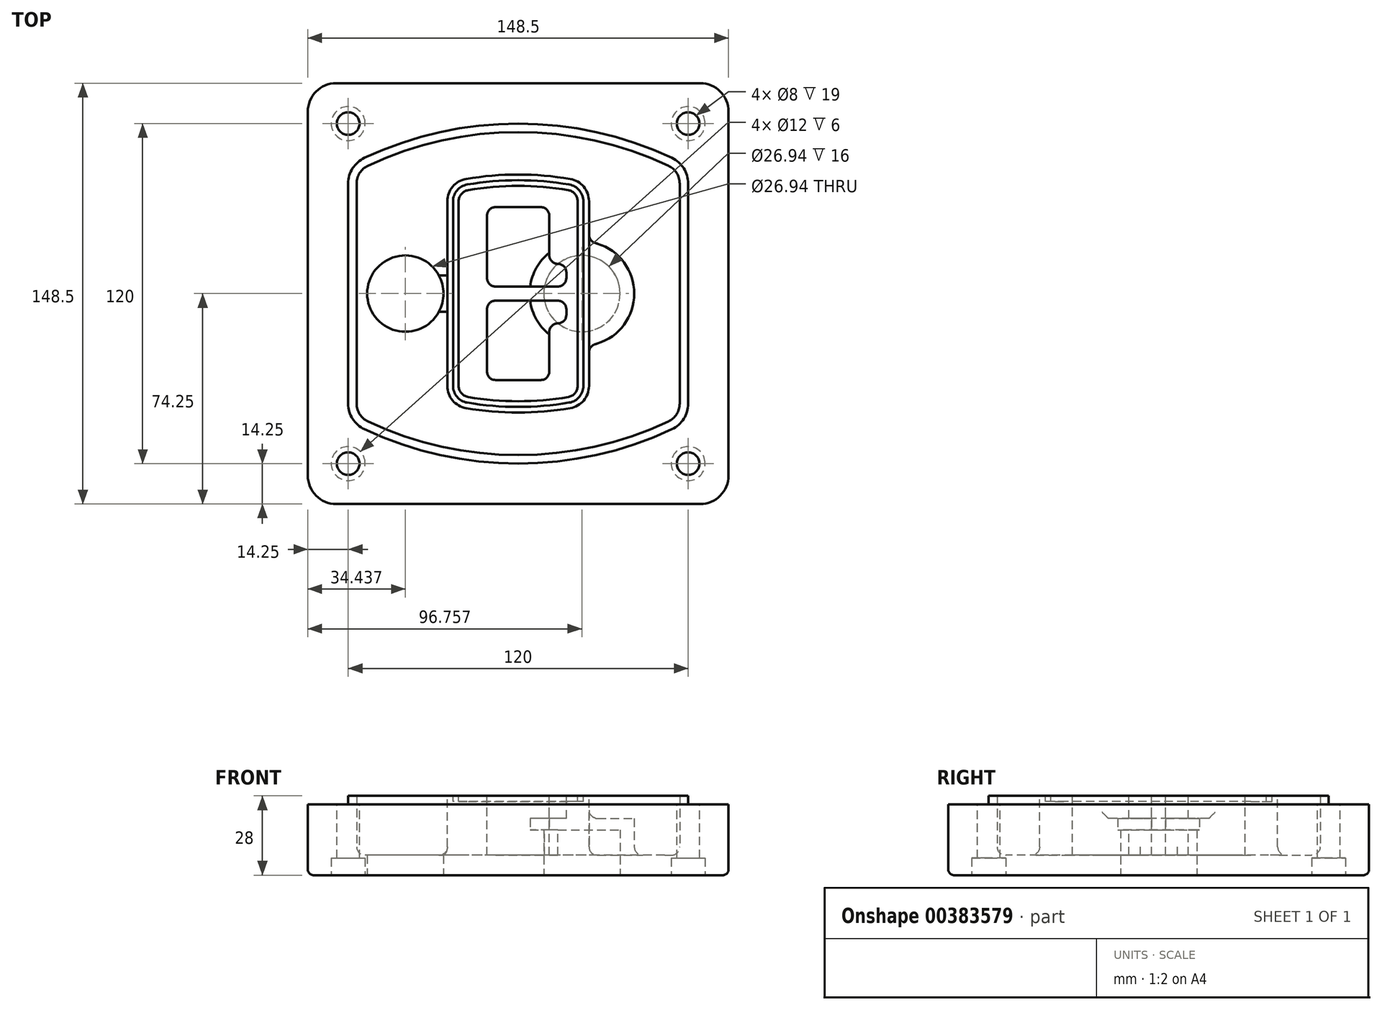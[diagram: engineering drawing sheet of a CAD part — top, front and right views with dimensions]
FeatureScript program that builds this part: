
annotation { "Feature Type Name" : "Feature", "Feature Type Description" : "" }
export const myFeature = defineFeature(function(context is Context, id is Id, definition is map)
    precondition{}
    {
        {
            var Q0;
            Q0=qCreatedBy(makeId("Top.planeOp"),FACE);
            var sketch = newSketch(context, id + "F0", { "sketchPlane" : qUnion([Q0])});
            skPoint(sketch, "E0.rect.middle", {"position": v(0, 0) * mm});
            skLineSegment(sketch, "E1.bottom", {"start": v(-64.25, -74.25) * mm, "end": v(64.25, -74.25) * mm});
            skLineSegment(sketch, "E1.top", {"start": v(-64.25, 74.25) * mm, "end": v(64.25, 74.25) * mm});
            skLineSegment(sketch, "E1.left", {"start": v(-74.25, -64.25) * mm, "end": v(-74.25, 64.25) * mm});
            skLineSegment(sketch, "E1.right", {"start": v(74.25, -64.25) * mm, "end": v(74.25, 64.25) * mm});
            skLineSegment(sketch, "E2", {"start": v(-74.25, 74.25) * mm, "end": v(74.25, -74.25) * mm, "construction": true});
            skLineSegment(sketch, "E3", {"start": v(74.25, 74.25) * mm, "end": v(-74.25, -74.25) * mm, "construction": true});
            skCircle(sketch, "E4", {"center": v(-60, 60) * mm, "radius": 4 * mm});
            skCircle(sketch, "E5", {"center": v(60, 60) * mm, "radius": 4 * mm});
            skCircle(sketch, "E6", {"center": v(60, -60) * mm, "radius": 4 * mm});
            skCircle(sketch, "E7", {"center": v(-60, -60) * mm, "radius": 4 * mm});
            skLineSegment(sketch, "E8", {"start": v(-60, 60) * mm, "end": v(60, 60) * mm, "construction": true});
            skLineSegment(sketch, "E9", {"start": v(60, 60) * mm, "end": v(60, -60) * mm, "construction": true});
            skLineSegment(sketch, "E10", {"start": v(60, -60) * mm, "end": v(-60, -60) * mm, "construction": true});
            skLineSegment(sketch, "E11", {"start": v(-60, -60) * mm, "end": v(-60, 60) * mm, "construction": true});
            skLineSegment(sketch, "E12", {"start": v(-60, 38.83) * mm, "end": v(-60, -38.83) * mm});
            skLineSegment(sketch, "E13", {"start": v(60, 38.83) * mm, "end": v(60, -38.83) * mm});
            skArc(sketch, "E14", {"start": v(54.26, 47.88) * mm, "mid": v(0, 60) * mm, "end": v(-54.26, 47.88) * mm});
            skArc(sketch, "E15", {"start": v(-54.26, -47.88) * mm, "mid": v(0, -60) * mm, "end": v(54.26, -47.88) * mm});
            skLineSegment(sketch, "E16", {"start": v(-60, 0) * mm, "end": v(60, 0) * mm, "construction": true});
            skPoint(sketch, "E17.visualSharp", {"position": v(-60, -45) * mm});
            skArc(sketch, "E17.filletArc", {"start": v(-60, -38.83) * mm, "mid": v(-58.44, -44.2) * mm, "end": v(-54.26, -47.88) * mm});
            skPoint(sketch, "E18.visualSharp", {"position": v(-60, 45) * mm});
            skArc(sketch, "E18.filletArc", {"start": v(-54.26, 47.88) * mm, "mid": v(-58.44, 44.2) * mm, "end": v(-60, 38.83) * mm});
            skPoint(sketch, "E19.visualSharp", {"position": v(60, 45) * mm});
            skArc(sketch, "E19.filletArc", {"start": v(60, 38.83) * mm, "mid": v(58.44, 44.2) * mm, "end": v(54.26, 47.88) * mm});
            skPoint(sketch, "E20.visualSharp", {"position": v(60, -45) * mm});
            skArc(sketch, "E20.filletArc", {"start": v(54.26, -47.88) * mm, "mid": v(58.44, -44.2) * mm, "end": v(60, -38.83) * mm});
            skPoint(sketch, "E21.visualSharp", {"position": v(-74.25, 74.25) * mm});
            skArc(sketch, "E21.filletArc", {"start": v(-64.25, 74.25) * mm, "mid": v(-71.32, 71.32) * mm, "end": v(-74.25, 64.25) * mm});
            skPoint(sketch, "E22.visualSharp", {"position": v(74.25, 74.25) * mm});
            skArc(sketch, "E22.filletArc", {"start": v(74.25, 64.25) * mm, "mid": v(71.32, 71.32) * mm, "end": v(64.25, 74.25) * mm});
            skPoint(sketch, "E23.visualSharp", {"position": v(74.25, -74.25) * mm});
            skArc(sketch, "E23.filletArc", {"start": v(64.25, -74.25) * mm, "mid": v(71.32, -71.32) * mm, "end": v(74.25, -64.25) * mm});
            skPoint(sketch, "E24.visualSharp", {"position": v(-74.25, -74.25) * mm});
            skArc(sketch, "E24.filletArc", {"start": v(-74.25, -64.25) * mm, "mid": v(-71.32, -71.32) * mm, "end": v(-64.25, -74.25) * mm});
            skArc(sketch, "E25.0", {"start": v(57, 38.83) * mm, "mid": v(55.9, 42.58) * mm, "end": v(52.98, 45.17) * mm});
            skLineSegment(sketch, "E25.1", {"start": v(57, 38.83) * mm, "end": v(57, -38.83) * mm});
            skArc(sketch, "E25.2", {"start": v(52.98, -45.17) * mm, "mid": v(55.9, -42.58) * mm, "end": v(57, -38.83) * mm});
            skArc(sketch, "E25.3", {"start": v(-52.98, -45.17) * mm, "mid": v(0, -57) * mm, "end": v(52.98, -45.17) * mm});
            skArc(sketch, "E25.4", {"start": v(-57, -38.83) * mm, "mid": v(-55.9, -42.58) * mm, "end": v(-52.98, -45.17) * mm});
            skArc(sketch, "E25.5", {"start": v(52.98, 45.17) * mm, "mid": v(0, 57) * mm, "end": v(-52.98, 45.17) * mm});
            skLineSegment(sketch, "E25.6", {"start": v(-57, 38.83) * mm, "end": v(-57, -38.83) * mm});
            skArc(sketch, "E25.7", {"start": v(-52.98, 45.17) * mm, "mid": v(-55.9, 42.58) * mm, "end": v(-57, 38.83) * mm});
            skArc(sketch, "E26.0", {"start": v(-55.96, 51.5) * mm, "mid": v(-61.82, 46.33) * mm, "end": v(-64, 38.83) * mm});
            skArc(sketch, "E26.1", {"start": v(55.96, 51.5) * mm, "mid": v(0, 64) * mm, "end": v(-55.96, 51.5) * mm});
            skArc(sketch, "E26.2", {"start": v(64, 38.83) * mm, "mid": v(61.82, 46.33) * mm, "end": v(55.96, 51.5) * mm});
            skLineSegment(sketch, "E26.3", {"start": v(64, 38.83) * mm, "end": v(64, -38.83) * mm});
            skArc(sketch, "E26.4", {"start": v(55.96, -51.5) * mm, "mid": v(61.82, -46.33) * mm, "end": v(64, -38.83) * mm});
            skLineSegment(sketch, "E26.5", {"start": v(-64, 38.83) * mm, "end": v(-64, -38.83) * mm});
            skArc(sketch, "E26.6", {"start": v(-55.96, -51.5) * mm, "mid": v(0, -64) * mm, "end": v(55.96, -51.5) * mm});
            skArc(sketch, "E26.7", {"start": v(-64, -38.83) * mm, "mid": v(-61.82, -46.33) * mm, "end": v(-55.96, -51.5) * mm});
            skSolve(sketch);
        }
        {
            var Q0;
            Q0=makeQuery(id+"F0.imprint","IMPRINT",FACE,{"disambiguationData":[TD([[makeQuery(id+"F0.imprint","IMPRINT",EDGE,{"derivedFrom":sQuery(id+"F0.wireOp",EDGE,"E1.bottom")}),1.0]])]});
            var Q1;
            Q1=makeQuery(id+"F0.imprint","IMPRINT",FACE,{"disambiguationData":[TD([[makeQuery(id+"F0.imprint","IMPRINT",EDGE,{"derivedFrom":sQuery(id+"F0.wireOp",EDGE,"E12")}),1.0]])]});
            var Q2;
            Q2=makeQuery(id+"F0.imprint","IMPRINT",FACE,{"disambiguationData":[TD([[makeQuery(id+"F0.imprint","IMPRINT",EDGE,{"derivedFrom":sQuery(id+"F0.wireOp",EDGE,"E25.0")}),1.0]])]});
            var Q3;
            Q3=makeQuery(id+"F0.imprint","IMPRINT",FACE,{"disambiguationData":[TD([[makeQuery(id+"F0.imprint","IMPRINT",EDGE,{"derivedFrom":sQuery(id+"F0.wireOp",EDGE,"E12")}),-1.0]])]});
            extrude(context, id + "F1", {"entities" : qUnion([Q0, Q1, Q2, Q3]), "oppositeDirection" : true, "depth" : 25 * mm});
        }
        {
            var Q0;
            Q0=makeQuery(id+"F0.imprint","IMPRINT",FACE,{"disambiguationData":[TD([[makeQuery(id+"F0.imprint","IMPRINT",EDGE,{"derivedFrom":sQuery(id+"F0.wireOp",EDGE,"E12")}),1.0]])]});
            extrude(context, id + "F2", {"entities" : qUnion([Q0]), "operationType" : NewBodyOperationType.ADD, "depth" : 3 * mm});
        }
        {
            var Q0;
            Q0=makeQuery(id+"F0.imprint","IMPRINT",FACE,{"disambiguationData":[TD([[makeQuery(id+"F0.imprint","IMPRINT",EDGE,{"derivedFrom":sQuery(id+"F0.wireOp",EDGE,"E25.0")}),1.0]])]});
            extrude(context, id + "F3", {"entities" : qUnion([Q0]), "operationType" : NewBodyOperationType.REMOVE, "oppositeDirection" : true, "depth" : 18 * mm});
        }
        {
            var Q0;
            Q0=makeQuery(id+"F2.opExtrude","CAP_FACE",FACE,{"disambiguationData":[OSD([sQuery(id+"F0.wireOp",EDGE,"E12"),sQuery(id+"F0.wireOp",EDGE,"E13"),sQuery(id+"F0.wireOp",EDGE,"E14"),sQuery(id+"F0.wireOp",EDGE,"E15"),sQuery(id+"F0.wireOp",EDGE,"E17.filletArc"),sQuery(id+"F0.wireOp",EDGE,"E18.filletArc"),sQuery(id+"F0.wireOp",EDGE,"E19.filletArc"),sQuery(id+"F0.wireOp",EDGE,"E20.filletArc"),sQuery(id+"F0.wireOp",EDGE,"E25.0"),sQuery(id+"F0.wireOp",EDGE,"E25.1"),sQuery(id+"F0.wireOp",EDGE,"E25.2"),sQuery(id+"F0.wireOp",EDGE,"E25.3"),sQuery(id+"F0.wireOp",EDGE,"E25.4"),sQuery(id+"F0.wireOp",EDGE,"E25.5"),sQuery(id+"F0.wireOp",EDGE,"E25.6"),sQuery(id+"F0.wireOp",EDGE,"E25.7")])],"isStart":false});
            var sketch = newSketch(context, id + "F4", { "sketchPlane" : qUnion([Q0])});
            skArc(sketch, "E27.0", {"start": v(-18.34, -40.45) * mm, "mid": v(0, -42) * mm, "end": v(18.34, -40.45) * mm});
            skArc(sketch, "E28.0", {"start": v(18.34, 40.45) * mm, "mid": v(0, 42) * mm, "end": v(-18.34, 40.45) * mm});
            skLineSegment(sketch, "E29", {"start": v(-25, 32.57) * mm, "end": v(-25, -32.57) * mm});
            skLineSegment(sketch, "E30", {"start": v(25, 32.57) * mm, "end": v(25, -32.57) * mm});
            skLineSegment(sketch, "E31", {"start": v(-25, 39.1) * mm, "end": v(25, 39.1) * mm, "construction": true});
            skLineSegment(sketch, "E32", {"start": v(-25, -39.1) * mm, "end": v(25, -39.1) * mm, "construction": true});
            skPoint(sketch, "E33.visualSharp", {"position": v(-25, 39.1) * mm});
            skArc(sketch, "E33.filletArc", {"start": v(-18.34, 40.45) * mm, "mid": v(-23.11, 37.73) * mm, "end": v(-25, 32.57) * mm});
            skPoint(sketch, "E34.visualSharp", {"position": v(25, 39.1) * mm});
            skArc(sketch, "E34.filletArc", {"start": v(25, 32.57) * mm, "mid": v(23.11, 37.73) * mm, "end": v(18.34, 40.45) * mm});
            skPoint(sketch, "E35.visualSharp", {"position": v(25, -39.1) * mm});
            skArc(sketch, "E35.filletArc", {"start": v(18.34, -40.45) * mm, "mid": v(23.11, -37.73) * mm, "end": v(25, -32.57) * mm});
            skPoint(sketch, "E36.visualSharp", {"position": v(-25, -39.1) * mm});
            skArc(sketch, "E36.filletArc", {"start": v(-25, -32.57) * mm, "mid": v(-23.11, -37.73) * mm, "end": v(-18.34, -40.45) * mm});
            skArc(sketch, "E37.0", {"start": v(52.98, 45.17) * mm, "mid": v(0, 57) * mm, "end": v(-52.98, 45.17) * mm});
            skArc(sketch, "E37.1", {"start": v(-52.98, 45.17) * mm, "mid": v(-55.9, 42.58) * mm, "end": v(-57, 38.83) * mm});
            skLineSegment(sketch, "E37.2", {"start": v(-57, 38.83) * mm, "end": v(-57, -38.83) * mm});
            skArc(sketch, "E37.3", {"start": v(-57, -38.83) * mm, "mid": v(-55.9, -42.58) * mm, "end": v(-52.98, -45.17) * mm});
            skArc(sketch, "E37.4", {"start": v(-52.98, -45.17) * mm, "mid": v(0, -57) * mm, "end": v(52.98, -45.17) * mm});
            skArc(sketch, "E37.5", {"start": v(52.98, -45.17) * mm, "mid": v(55.9, -42.58) * mm, "end": v(57, -38.83) * mm});
            skLineSegment(sketch, "E37.6", {"start": v(57, 38.83) * mm, "end": v(57, -38.83) * mm});
            skArc(sketch, "E37.7", {"start": v(57, 38.83) * mm, "mid": v(55.9, 42.58) * mm, "end": v(52.98, 45.17) * mm});
            skLineSegment(sketch, "E38.0", {"start": v(23, 32.57) * mm, "end": v(23, -32.57) * mm});
            skArc(sketch, "E38.1", {"start": v(18, -38.48) * mm, "mid": v(21.58, -36.44) * mm, "end": v(23, -32.57) * mm});
            skArc(sketch, "E38.2", {"start": v(-18, -38.48) * mm, "mid": v(0, -40) * mm, "end": v(18, -38.48) * mm});
            skArc(sketch, "E38.3", {"start": v(-23, -32.57) * mm, "mid": v(-21.58, -36.44) * mm, "end": v(-18, -38.48) * mm});
            skLineSegment(sketch, "E38.4", {"start": v(-23, 32.57) * mm, "end": v(-23, -32.57) * mm});
            skArc(sketch, "E38.5", {"start": v(23, 32.57) * mm, "mid": v(21.58, 36.44) * mm, "end": v(18, 38.48) * mm});
            skArc(sketch, "E38.6", {"start": v(-18, 38.48) * mm, "mid": v(-21.58, 36.44) * mm, "end": v(-23, 32.57) * mm});
            skArc(sketch, "E38.7", {"start": v(18, 38.48) * mm, "mid": v(0, 40) * mm, "end": v(-18, 38.48) * mm});
            skArc(sketch, "E39.0", {"start": v(21, 32.57) * mm, "mid": v(20.06, 35.15) * mm, "end": v(17.67, 36.5) * mm});
            skLineSegment(sketch, "E39.1", {"start": v(21, 32.57) * mm, "end": v(21, -32.57) * mm});
            skArc(sketch, "E39.2", {"start": v(17.67, -36.5) * mm, "mid": v(20.06, -35.15) * mm, "end": v(21, -32.57) * mm});
            skArc(sketch, "E39.3", {"start": v(-17.67, -36.5) * mm, "mid": v(0, -38) * mm, "end": v(17.67, -36.5) * mm});
            skArc(sketch, "E39.4", {"start": v(-21, -32.57) * mm, "mid": v(-20.06, -35.15) * mm, "end": v(-17.67, -36.5) * mm});
            skArc(sketch, "E39.5", {"start": v(17.67, 36.5) * mm, "mid": v(0, 38) * mm, "end": v(-17.67, 36.5) * mm});
            skLineSegment(sketch, "E39.6", {"start": v(-21, 32.57) * mm, "end": v(-21, -32.57) * mm});
            skArc(sketch, "E39.7", {"start": v(-17.67, 36.5) * mm, "mid": v(-20.06, 35.15) * mm, "end": v(-21, 32.57) * mm});
            skLineSegment(sketch, "E40", {"start": v(-25, 0) * mm, "end": v(25, 0) * mm, "construction": true});
            skLineSegment(sketch, "E41", {"start": v(-11, 5.5) * mm, "end": v(-11, 27.5) * mm});
            skLineSegment(sketch, "E42", {"start": v(-8, 30.5) * mm, "end": v(8, 30.5) * mm});
            skLineSegment(sketch, "E43", {"start": v(11, 27.5) * mm, "end": v(11, 13.5) * mm});
            skLineSegment(sketch, "E44", {"start": v(14, 10.5) * mm, "end": v(14, 10.5) * mm});
            skLineSegment(sketch, "E45", {"start": v(17, 7.5) * mm, "end": v(17, 5.5) * mm});
            skLineSegment(sketch, "E46", {"start": v(14, 2.5) * mm, "end": v(-8, 2.5) * mm});
            skPoint(sketch, "E47.visualSharp", {"position": v(-11, 30.5) * mm});
            skArc(sketch, "E47.filletArc", {"start": v(-8, 30.5) * mm, "mid": v(-10.12, 29.62) * mm, "end": v(-11, 27.5) * mm});
            skPoint(sketch, "E48.visualSharp", {"position": v(11, 30.5) * mm});
            skArc(sketch, "E48.filletArc", {"start": v(11, 27.5) * mm, "mid": v(10.12, 29.62) * mm, "end": v(8, 30.5) * mm});
            skPoint(sketch, "E49.visualSharp", {"position": v(11, 10.5) * mm});
            skArc(sketch, "E49.filletArc", {"start": v(11, 13.5) * mm, "mid": v(11.88, 11.38) * mm, "end": v(14, 10.5) * mm});
            skPoint(sketch, "E50.visualSharp", {"position": v(17, 10.5) * mm});
            skArc(sketch, "E50.filletArc", {"start": v(17, 7.5) * mm, "mid": v(16.12, 9.62) * mm, "end": v(14, 10.5) * mm});
            skPoint(sketch, "E51.visualSharp", {"position": v(17, 2.5) * mm});
            skArc(sketch, "E51.filletArc", {"start": v(14, 2.5) * mm, "mid": v(16.12, 3.38) * mm, "end": v(17, 5.5) * mm});
            skPoint(sketch, "E52.visualSharp", {"position": v(-11, 2.5) * mm});
            skArc(sketch, "E52.filletArc", {"start": v(-11, 5.5) * mm, "mid": v(-10.12, 3.38) * mm, "end": v(-8, 2.5) * mm});
            skLineSegment(sketch, "E53.0.MirrorCS", {"start": v(14, -2.5) * mm, "end": v(-8, -2.5) * mm});
            skArc(sketch, "E54.0.MirrorCS", {"start": v(-11, -5.5) * mm, "mid": v(-10.12, -3.38) * mm, "end": v(-8, -2.5) * mm});
            skLineSegment(sketch, "E55.0.MirrorCS", {"start": v(-11, -5.5) * mm, "end": v(-11, -27.5) * mm});
            skArc(sketch, "E56.0.MirrorCS", {"start": v(-8, -30.5) * mm, "mid": v(-10.12, -29.62) * mm, "end": v(-11, -27.5) * mm});
            skLineSegment(sketch, "E57.0.MirrorCS", {"start": v(-8, -30.5) * mm, "end": v(8, -30.5) * mm});
            skArc(sketch, "E58.0.MirrorCS", {"start": v(11, -27.5) * mm, "mid": v(10.12, -29.62) * mm, "end": v(8, -30.5) * mm});
            skLineSegment(sketch, "E59.0.MirrorCS", {"start": v(11, -27.5) * mm, "end": v(11, -13.5) * mm});
            skArc(sketch, "E60.0.MirrorCS", {"start": v(11, -13.5) * mm, "mid": v(11.88, -11.38) * mm, "end": v(14, -10.5) * mm});
            skArc(sketch, "E61.0.MirrorCS", {"start": v(17, -7.5) * mm, "mid": v(16.12, -9.62) * mm, "end": v(14, -10.5) * mm});
            skLineSegment(sketch, "E62.0.MirrorCS", {"start": v(17, -7.5) * mm, "end": v(17, -5.5) * mm});
            skArc(sketch, "E63.0.MirrorCS", {"start": v(14, -2.5) * mm, "mid": v(16.12, -3.38) * mm, "end": v(17, -5.5) * mm});
            skSolve(sketch);
        }
        {
            var Q0;
            Q0=makeQuery(id+"F4.imprint","IMPRINT",FACE,{"disambiguationData":[TD([[makeQuery(id+"F4.imprint","IMPRINT",EDGE,{"derivedFrom":sQuery(id+"F4.wireOp",EDGE,"E27.0")}),1.0]])]});
            var Q1;
            Q1=makeQuery(id+"F4.imprint","IMPRINT",FACE,{"disambiguationData":[TD([[makeQuery(id+"F4.imprint","IMPRINT",EDGE,{"derivedFrom":sQuery(id+"F4.wireOp",EDGE,"E38.0")}),-1.0]])]});
            var Q2;
            Q2=makeQuery(id+"F4.imprint","IMPRINT",FACE,{"disambiguationData":[TD([[makeQuery(id+"F4.imprint","IMPRINT",EDGE,{"derivedFrom":sQuery(id+"F4.wireOp",EDGE,"E39.0")}),1.0]])]});
            extrude(context, id + "F5", {"entities" : qUnion([Q0, Q1, Q2]), "operationType" : NewBodyOperationType.ADD, "endBound" : BoundingType.UP_TO_NEXT, "oppositeDirection" : true, "depth" : 25 * mm});
        }
        {
            var Q0;
            Q0=makeQuery(id+"F4.imprint","IMPRINT",FACE,{"disambiguationData":[TD([[makeQuery(id+"F4.imprint","IMPRINT",EDGE,{"derivedFrom":sQuery(id+"F4.wireOp",EDGE,"E38.0")}),-1.0]])]});
            extrude(context, id + "F6", {"entities" : qUnion([Q0]), "operationType" : NewBodyOperationType.REMOVE, "oppositeDirection" : true, "depth" : 2 * mm});
        }
        {
            var Q0;
            Q0=makeQuery(id+"F1.opExtrude","CAP_FACE",FACE,{"disambiguationData":[OSD([sQuery(id+"F0.wireOp",EDGE,"E1.bottom"),sQuery(id+"F0.wireOp",EDGE,"E1.top"),sQuery(id+"F0.wireOp",EDGE,"E1.left"),sQuery(id+"F0.wireOp",EDGE,"E1.right"),sQuery(id+"F0.wireOp",EDGE,"E4"),sQuery(id+"F0.wireOp",EDGE,"E5"),sQuery(id+"F0.wireOp",EDGE,"E6"),sQuery(id+"F0.wireOp",EDGE,"E7"),sQuery(id+"F0.wireOp",EDGE,"E21.filletArc"),sQuery(id+"F0.wireOp",EDGE,"E22.filletArc"),sQuery(id+"F0.wireOp",EDGE,"E23.filletArc"),sQuery(id+"F0.wireOp",EDGE,"E24.filletArc")])],"isStart":false});
            var sketch = newSketch(context, id + "F7", { "sketchPlane" : qUnion([Q0])});
            skCircle(sketch, "E64", {"center": v(22.5, 0) * mm, "radius": 13.47 * mm});
            skCircle(sketch, "E65", {"center": v(-39.81, 0) * mm, "radius": 13.47 * mm});
            skLineSegment(sketch, "E66", {"start": v(74.25, 0) * mm, "end": v(-74.25, 0) * mm});
            skCircle(sketch, "E67", {"center": v(22.5, 0) * mm, "radius": 18.47 * mm});
            skCircle(sketch, "E68", {"center": v(60, -60) * mm, "radius": 6 * mm});
            skCircle(sketch, "E69", {"center": v(-60, -60) * mm, "radius": 6 * mm});
            skCircle(sketch, "E70", {"center": v(-60, 60) * mm, "radius": 6 * mm});
            skCircle(sketch, "E71", {"center": v(60, 60) * mm, "radius": 6 * mm});
            skSolve(sketch);
        }
        {
            var Q0;
            {var subQ1=sQuery(id+"F7.wireOp",EDGE,"E66");var subQ4=sQuery(id+"F7.wireOp",EDGE,"E64");var subQ6=makeQuery(id+"F7.imprint","INTERSECT",VERTEX,{"disambiguationData":[OD(0.0)],"derivedFrom":[subQ4,subQ1]});Q0=makeQuery(id+"F7.imprint","IMPRINT",FACE,{"disambiguationData":[TD([[makeQuery(id+"F7.imprint","IMPRINT",EDGE,{"disambiguationData":[TD([[subQ6,-1.0]])],"derivedFrom":subQ4}),-1.0]])]});}
            var Q1;
            {var subQ0=sQuery(id+"F7.wireOp",EDGE,"E66");var subQ1=sQuery(id+"F7.wireOp",EDGE,"E64");var subQ3=makeQuery(id+"F7.imprint","INTERSECT",VERTEX,{"disambiguationData":[OD(0.0)],"derivedFrom":[subQ1,subQ0]});Q1=makeQuery(id+"F7.imprint","IMPRINT",FACE,{"disambiguationData":[TD([[makeQuery(id+"F7.imprint","IMPRINT",EDGE,{"disambiguationData":[TD([[subQ3,-1.0]])],"derivedFrom":subQ1}),1.0]])]});}
            var Q2;
            {var subQ0=sQuery(id+"F7.wireOp",EDGE,"E66");var subQ1=sQuery(id+"F7.wireOp",EDGE,"E64");var subQ3=makeQuery(id+"F7.imprint","INTERSECT",VERTEX,{"disambiguationData":[OD(0.0)],"derivedFrom":[subQ1,subQ0]});Q2=makeQuery(id+"F7.imprint","IMPRINT",FACE,{"disambiguationData":[TD([[makeQuery(id+"F7.imprint","IMPRINT",EDGE,{"disambiguationData":[TD([[subQ3,1.0]])],"derivedFrom":subQ1}),1.0]])]});}
            var Q3;
            {var subQ1=sQuery(id+"F7.wireOp",EDGE,"E66");var subQ4=sQuery(id+"F7.wireOp",EDGE,"E64");var subQ6=makeQuery(id+"F7.imprint","INTERSECT",VERTEX,{"disambiguationData":[OD(0.0)],"derivedFrom":[subQ4,subQ1]});Q3=makeQuery(id+"F7.imprint","IMPRINT",FACE,{"disambiguationData":[TD([[makeQuery(id+"F7.imprint","IMPRINT",EDGE,{"disambiguationData":[TD([[subQ6,1.0]])],"derivedFrom":subQ4}),-1.0]])]});}
            extrude(context, id + "F8", {"entities" : qUnion([Q0, Q1, Q2, Q3]), "operationType" : NewBodyOperationType.ADD, "oppositeDirection" : true, "depth" : 20 * mm});
        }
        {
            var Q0;
            {var subQ0=sQuery(id+"F7.wireOp",EDGE,"E66");var subQ1=sQuery(id+"F7.wireOp",EDGE,"E64");var subQ3=makeQuery(id+"F7.imprint","INTERSECT",VERTEX,{"disambiguationData":[OD(0.0)],"derivedFrom":[subQ1,subQ0]});Q0=makeQuery(id+"F7.imprint","IMPRINT",FACE,{"disambiguationData":[TD([[makeQuery(id+"F7.imprint","IMPRINT",EDGE,{"disambiguationData":[TD([[subQ3,-1.0]])],"derivedFrom":subQ1}),1.0]])]});}
            var Q1;
            {var subQ0=sQuery(id+"F7.wireOp",EDGE,"E66");var subQ1=sQuery(id+"F7.wireOp",EDGE,"E64");var subQ3=makeQuery(id+"F7.imprint","INTERSECT",VERTEX,{"disambiguationData":[OD(0.0)],"derivedFrom":[subQ1,subQ0]});Q1=makeQuery(id+"F7.imprint","IMPRINT",FACE,{"disambiguationData":[TD([[makeQuery(id+"F7.imprint","IMPRINT",EDGE,{"disambiguationData":[TD([[subQ3,1.0]])],"derivedFrom":subQ1}),1.0]])]});}
            extrude(context, id + "F9", {"entities" : qUnion([Q0, Q1]), "operationType" : NewBodyOperationType.REMOVE, "oppositeDirection" : true, "depth" : 16 * mm});
        }
        {
            var Q0;
            {var subQ0=sQuery(id+"F7.wireOp",EDGE,"E66");var subQ1=sQuery(id+"F7.wireOp",EDGE,"E65");var subQ3=makeQuery(id+"F7.imprint","INTERSECT",VERTEX,{"disambiguationData":[OD(0.0)],"derivedFrom":[subQ1,subQ0]});Q0=makeQuery(id+"F7.imprint","IMPRINT",FACE,{"disambiguationData":[TD([[makeQuery(id+"F7.imprint","IMPRINT",EDGE,{"disambiguationData":[TD([[subQ3,-1.0]])],"derivedFrom":subQ1}),1.0]])]});}
            var Q1;
            {var subQ0=sQuery(id+"F7.wireOp",EDGE,"E66");var subQ1=sQuery(id+"F7.wireOp",EDGE,"E65");var subQ3=makeQuery(id+"F7.imprint","INTERSECT",VERTEX,{"disambiguationData":[OD(0.0)],"derivedFrom":[subQ1,subQ0]});Q1=makeQuery(id+"F7.imprint","IMPRINT",FACE,{"disambiguationData":[TD([[makeQuery(id+"F7.imprint","IMPRINT",EDGE,{"disambiguationData":[TD([[subQ3,1.0]])],"derivedFrom":subQ1}),1.0]])]});}
            extrude(context, id + "F10", {"entities" : qUnion([Q0, Q1]), "operationType" : NewBodyOperationType.REMOVE, "oppositeDirection" : true, "depth" : 25 * mm});
        }
        {
            var Q0;
            Q0=makeQuery(id+"F7.imprint","IMPRINT",FACE,{"disambiguationData":[TD([[makeQuery(id+"F7.imprint","IMPRINT",EDGE,{"derivedFrom":sQuery(id+"F7.wireOp",EDGE,"E68")}),1.0]])]});
            var Q1;
            Q1=makeQuery(id+"F7.imprint","IMPRINT",FACE,{"disambiguationData":[TD([[makeQuery(id+"F7.imprint","IMPRINT",EDGE,{"derivedFrom":makeQuery(id+"F1.opExtrude","CAP_EDGE",EDGE,{"disambiguationData":[OSD([sQuery(id+"F0.wireOp",EDGE,"E5")])],"isStart":false})}),-1.0]])]});
            var Q2;
            Q2=makeQuery(id+"F7.imprint","IMPRINT",FACE,{"disambiguationData":[TD([[makeQuery(id+"F7.imprint","IMPRINT",EDGE,{"derivedFrom":sQuery(id+"F7.wireOp",EDGE,"E69")}),1.0]])]});
            var Q3;
            Q3=makeQuery(id+"F7.imprint","IMPRINT",FACE,{"disambiguationData":[TD([[makeQuery(id+"F7.imprint","IMPRINT",EDGE,{"derivedFrom":makeQuery(id+"F1.opExtrude","CAP_EDGE",EDGE,{"disambiguationData":[OSD([sQuery(id+"F0.wireOp",EDGE,"E4")])],"isStart":false})}),-1.0]])]});
            var Q4;
            Q4=makeQuery(id+"F7.imprint","IMPRINT",FACE,{"disambiguationData":[TD([[makeQuery(id+"F7.imprint","IMPRINT",EDGE,{"derivedFrom":sQuery(id+"F7.wireOp",EDGE,"E70")}),1.0]])]});
            var Q5;
            Q5=makeQuery(id+"F7.imprint","IMPRINT",FACE,{"disambiguationData":[TD([[makeQuery(id+"F7.imprint","IMPRINT",EDGE,{"derivedFrom":makeQuery(id+"F1.opExtrude","CAP_EDGE",EDGE,{"disambiguationData":[OSD([sQuery(id+"F0.wireOp",EDGE,"E7")])],"isStart":false})}),-1.0]])]});
            var Q6;
            Q6=makeQuery(id+"F7.imprint","IMPRINT",FACE,{"disambiguationData":[TD([[makeQuery(id+"F7.imprint","IMPRINT",EDGE,{"derivedFrom":sQuery(id+"F7.wireOp",EDGE,"E71")}),1.0]])]});
            var Q7;
            Q7=makeQuery(id+"F7.imprint","IMPRINT",FACE,{"disambiguationData":[TD([[makeQuery(id+"F7.imprint","IMPRINT",EDGE,{"derivedFrom":makeQuery(id+"F1.opExtrude","CAP_EDGE",EDGE,{"disambiguationData":[OSD([sQuery(id+"F0.wireOp",EDGE,"E6")])],"isStart":false})}),-1.0]])]});
            extrude(context, id + "F11", {"entities" : qUnion([Q0, Q1, Q2, Q3, Q4, Q5, Q6, Q7]), "operationType" : NewBodyOperationType.REMOVE, "oppositeDirection" : true, "depth" : 6 * mm});
        }
        {
            var Q0;
            Q0=makeQuery(id+"F9.boolean.opBoolean","COPY",FACE,{"derivedFrom":makeQuery(id+"F9.opExtrude","CAP_FACE",FACE,{"disambiguationData":[OSD([sQuery(id+"F7.wireOp",EDGE,"E64")])],"isStart":false})});
            var sketch = newSketch(context, id + "F12", { "sketchPlane" : qUnion([Q0])});
            skArc(sketch, "E72.0", {"start": v(11, 14.45) * mm, "mid": v(6.45, 9.13) * mm, "end": v(4.2, 2.5) * mm});
            skArc(sketch, "E72.1", {"start": v(4.2, -2.5) * mm, "mid": v(6.45, -9.13) * mm, "end": v(11, -14.45) * mm});
            skLineSegment(sketch, "E73", {"start": v(4.2, -2.5) * mm, "end": v(14, -2.5) * mm});
            skLineSegment(sketch, "E74.0", {"start": v(14, 2.5) * mm, "end": v(4.2, 2.5) * mm});
            skArc(sketch, "E74.1", {"start": v(14, 2.5) * mm, "mid": v(16.12, 3.38) * mm, "end": v(17, 5.5) * mm});
            skLineSegment(sketch, "E74.2", {"start": v(17, 7.5) * mm, "end": v(17, 5.5) * mm});
            skArc(sketch, "E74.3", {"start": v(17, 7.5) * mm, "mid": v(16.12, 9.62) * mm, "end": v(14, 10.5) * mm});
            skArc(sketch, "E74.4", {"start": v(11, 13.5) * mm, "mid": v(11.88, 11.38) * mm, "end": v(14, 10.5) * mm});
            skLineSegment(sketch, "E74.5", {"start": v(11, 14.45) * mm, "end": v(11, 13.5) * mm});
            skLineSegment(sketch, "E74.7", {"start": v(14, -2.5) * mm, "end": v(4.2, -2.5) * mm});
            skArc(sketch, "E74.8", {"start": v(14, -2.5) * mm, "mid": v(16.12, -3.38) * mm, "end": v(17, -5.5) * mm});
            skLineSegment(sketch, "E74.9", {"start": v(17, -7.5) * mm, "end": v(17, -5.5) * mm});
            skArc(sketch, "E74.10", {"start": v(17, -7.5) * mm, "mid": v(16.12, -9.62) * mm, "end": v(14, -10.5) * mm});
            skArc(sketch, "E74.11", {"start": v(11, -13.5) * mm, "mid": v(11.88, -11.38) * mm, "end": v(14, -10.5) * mm});
            skLineSegment(sketch, "E74.12", {"start": v(11, -14.45) * mm, "end": v(11, -13.5) * mm});
            skPoint(sketch, "E75.orphan", {"position": v(11, -27.5) * mm});
            skPoint(sketch, "E76.orphan", {"position": v(-8, -2.5) * mm});
            skPoint(sketch, "E77.orphan", {"position": v(-8, 2.5) * mm});
            skPoint(sketch, "E78.orphan", {"position": v(11, 27.5) * mm});
            skSolve(sketch);
        }
        {
            var Q0;
            {var subQ7=sQuery(id+"F12.wireOp",EDGE,"E72.0");var subQ14=sQuery(id+"F12.wireOp",EDGE,"E72.1");var subQ16=sQuery(id+"F12.wireOp",EDGE,"E74.1");var subQ18=sQuery(id+"F12.wireOp",EDGE,"E74.8");Q0=qUnion([makeQuery(id+"F12.imprint","IMPRINT",FACE,{"disambiguationData":[TD([[makeQuery(id+"F12.imprint","IMPRINT",EDGE,{"derivedFrom":subQ7}),1.0]])]}),makeQuery(id+"F12.imprint","IMPRINT",FACE,{"disambiguationData":[TD([[makeQuery(id+"F12.imprint","IMPRINT",EDGE,{"derivedFrom":subQ14}),1.0]])]}),makeQuery(id+"F12.imprint","IMPRINT",FACE,{"disambiguationData":[TD([[makeQuery(id+"F12.imprint","IMPRINT",EDGE,{"derivedFrom":subQ16}),1.0]])]}),makeQuery(id+"F12.imprint","IMPRINT",FACE,{"disambiguationData":[TD([[makeQuery(id+"F12.imprint","IMPRINT",EDGE,{"derivedFrom":subQ18}),-1.0]])]})]);}
            var Q1;
            Q1=makeQuery(id+"F5.boolean.opBoolean","SPLIT",FACE,{"disambiguationData":[TD([makeQuery(id+"F5.opExtrude","SWEPT_FACE",FACE,{"disambiguationData":[OSD([sQuery(id+"F4.wireOp",EDGE,"E41")])]})])],"derivedFrom":makeQuery(id+"F3.boolean.opBoolean","COPY",FACE,{"derivedFrom":makeQuery(id+"F3.opExtrude","CAP_FACE",FACE,{"disambiguationData":[OSD([sQuery(id+"F0.wireOp",EDGE,"E25.0"),sQuery(id+"F0.wireOp",EDGE,"E25.1"),sQuery(id+"F0.wireOp",EDGE,"E25.2"),sQuery(id+"F0.wireOp",EDGE,"E25.3"),sQuery(id+"F0.wireOp",EDGE,"E25.4"),sQuery(id+"F0.wireOp",EDGE,"E25.5"),sQuery(id+"F0.wireOp",EDGE,"E25.6"),sQuery(id+"F0.wireOp",EDGE,"E25.7")])],"isStart":false})})});
            extrude(context, id + "F13", {"entities" : qUnion([Q0]), "operationType" : NewBodyOperationType.REMOVE, "endBound" : BoundingType.UP_TO_SURFACE, "endBoundEntityFace" : qUnion([Q1]), "depth" : 25 * mm});
        }
        {
            var Q0;
            Q0=makeQuery(id+"F3.boolean.opBoolean","COPY",EDGE,{"derivedFrom":makeQuery(id+"F3.opExtrude","CAP_EDGE",EDGE,{"disambiguationData":[OSD([sQuery(id+"F0.wireOp",EDGE,"E25.6")])],"isStart":false})});
            var Q1;
            Q1=makeQuery(id+"F8.boolean.opBoolean","INTERSECT",EDGE,{"derivedFrom":[makeQuery(id+"F5.opExtrude","SWEPT_FACE",FACE,{"disambiguationData":[OSD([sQuery(id+"F4.wireOp",EDGE,"E30")])]}),makeQuery(id+"F8.opExtrude","CAP_FACE",FACE,{"disambiguationData":[OSD([sQuery(id+"F7.wireOp",EDGE,"E67")])],"isStart":false})]});
            var Q2;
            Q2=makeQuery(id+"F8.boolean.opBoolean","INTERSECT",EDGE,{"disambiguationData":[OD(1.0)],"derivedFrom":[makeQuery(id+"F5.opExtrude","SWEPT_FACE",FACE,{"disambiguationData":[OSD([sQuery(id+"F4.wireOp",EDGE,"E30")])]}),makeQuery(id+"F8.opExtrude","SWEPT_FACE",FACE,{"disambiguationData":[OSD([sQuery(id+"F7.wireOp",EDGE,"E67")])]})]});
            var Q3;
            {var subQ0=sQuery(id+"F4.wireOp",EDGE,"E30");Q3=makeQuery(id+"F8.boolean.opBoolean","SPLIT",EDGE,{"disambiguationData":[TD([makeQuery(id+"F5.opExtrude","SWEPT_FACE",FACE,{"disambiguationData":[OSD([sQuery(id+"F4.wireOp",EDGE,"E35.filletArc")])]})])],"derivedFrom":makeQuery(id+"F5.opExtrude","CAP_EDGE",EDGE,{"disambiguationData":[OSD([subQ0])],"isStart":false})});}
            var Q4;
            {var subQ0=sQuery(id+"F0.wireOp",EDGE,"E25.7");var subQ1=sQuery(id+"F0.wireOp",EDGE,"E25.1");var subQ2=sQuery(id+"F0.wireOp",EDGE,"E25.6");var subQ3=sQuery(id+"F0.wireOp",EDGE,"E25.5");var subQ4=sQuery(id+"F0.wireOp",EDGE,"E25.4");var subQ5=sQuery(id+"F0.wireOp",EDGE,"E25.0");var subQ6=sQuery(id+"F0.wireOp",EDGE,"E25.2");var subQ7=sQuery(id+"F0.wireOp",EDGE,"E25.3");Q4=makeQuery(id+"F8.boolean.opBoolean","INTERSECT",EDGE,{"derivedFrom":[makeQuery(id+"F5.boolean.opBoolean","SPLIT",FACE,{"disambiguationData":[TD([makeQuery(id+"F2.opExtrude","SWEPT_FACE",FACE,{"disambiguationData":[OSD([subQ5])]})])],"derivedFrom":makeQuery(id+"F3.boolean.opBoolean","COPY",FACE,{"derivedFrom":makeQuery(id+"F3.opExtrude","CAP_FACE",FACE,{"disambiguationData":[OSD([subQ5,subQ1,subQ6,subQ7,subQ4,subQ3,subQ2,subQ0])],"isStart":false})})}),makeQuery(id+"F8.opExtrude","SWEPT_FACE",FACE,{"disambiguationData":[OSD([sQuery(id+"F7.wireOp",EDGE,"E67")])]})]});}
            var Q5;
            Q5=makeQuery(id+"F8.boolean.opBoolean","INTERSECT",EDGE,{"disambiguationData":[OD(0.0)],"derivedFrom":[makeQuery(id+"F5.opExtrude","SWEPT_FACE",FACE,{"disambiguationData":[OSD([sQuery(id+"F4.wireOp",EDGE,"E30")])]}),makeQuery(id+"F8.opExtrude","SWEPT_FACE",FACE,{"disambiguationData":[OSD([sQuery(id+"F7.wireOp",EDGE,"E67")])]})]});
            fillet(context, id + "F14", {"entities" : qUnion([Q0, Q1, Q2, Q3, Q4, Q5]), "radius" : 3 * mm, "tangentPropagation" : true, "allowEdgeOverflow" : false});
        }
        {
            var Q0;
            Q0=makeQuery(id+"F1.opExtrude","CAP_EDGE",EDGE,{"disambiguationData":[OSD([sQuery(id+"F0.wireOp",EDGE,"E1.bottom")])],"isStart":false});
            fillet(context, id + "F15", {"entities" : qUnion([Q0]), "radius" : 2 * mm, "tangentPropagation" : true, "allowEdgeOverflow" : false});
        }
        {
            var Q0;
            {var subQ0=sQuery(id+"F0.wireOp",EDGE,"E21.filletArc");var subQ1=sQuery(id+"F0.wireOp",EDGE,"E7");var subQ2=sQuery(id+"F0.wireOp",EDGE,"E6");var subQ3=sQuery(id+"F0.wireOp",EDGE,"E5");var subQ4=sQuery(id+"F0.wireOp",EDGE,"E4");var subQ5=sQuery(id+"F0.wireOp",EDGE,"E22.filletArc");var subQ6=sQuery(id+"F0.wireOp",EDGE,"E1.bottom");var subQ7=sQuery(id+"F0.wireOp",EDGE,"E1.right");var subQ8=sQuery(id+"F0.wireOp",EDGE,"E1.top");var subQ9=sQuery(id+"F0.wireOp",EDGE,"E1.left");var subQ10=sQuery(id+"F0.wireOp",EDGE,"E23.filletArc");var subQ11=sQuery(id+"F0.wireOp",EDGE,"E24.filletArc");Q0=makeQuery(id+"F2.boolean.opBoolean","SPLIT",FACE,{"disambiguationData":[TD([makeQuery(id+"F1.opExtrude","SWEPT_FACE",FACE,{"disambiguationData":[OSD([subQ6])]})])],"derivedFrom":makeQuery(id+"F1.opExtrude","CAP_FACE",FACE,{"disambiguationData":[OSD([subQ6,subQ8,subQ9,subQ7,subQ4,subQ3,subQ2,subQ1,subQ0,subQ5,subQ10,subQ11])],"isStart":true})});}
            var sketch = newSketch(context, id + "F16", { "sketchPlane" : qUnion([Q0])});
            skSolve(sketch);
        }
    });
